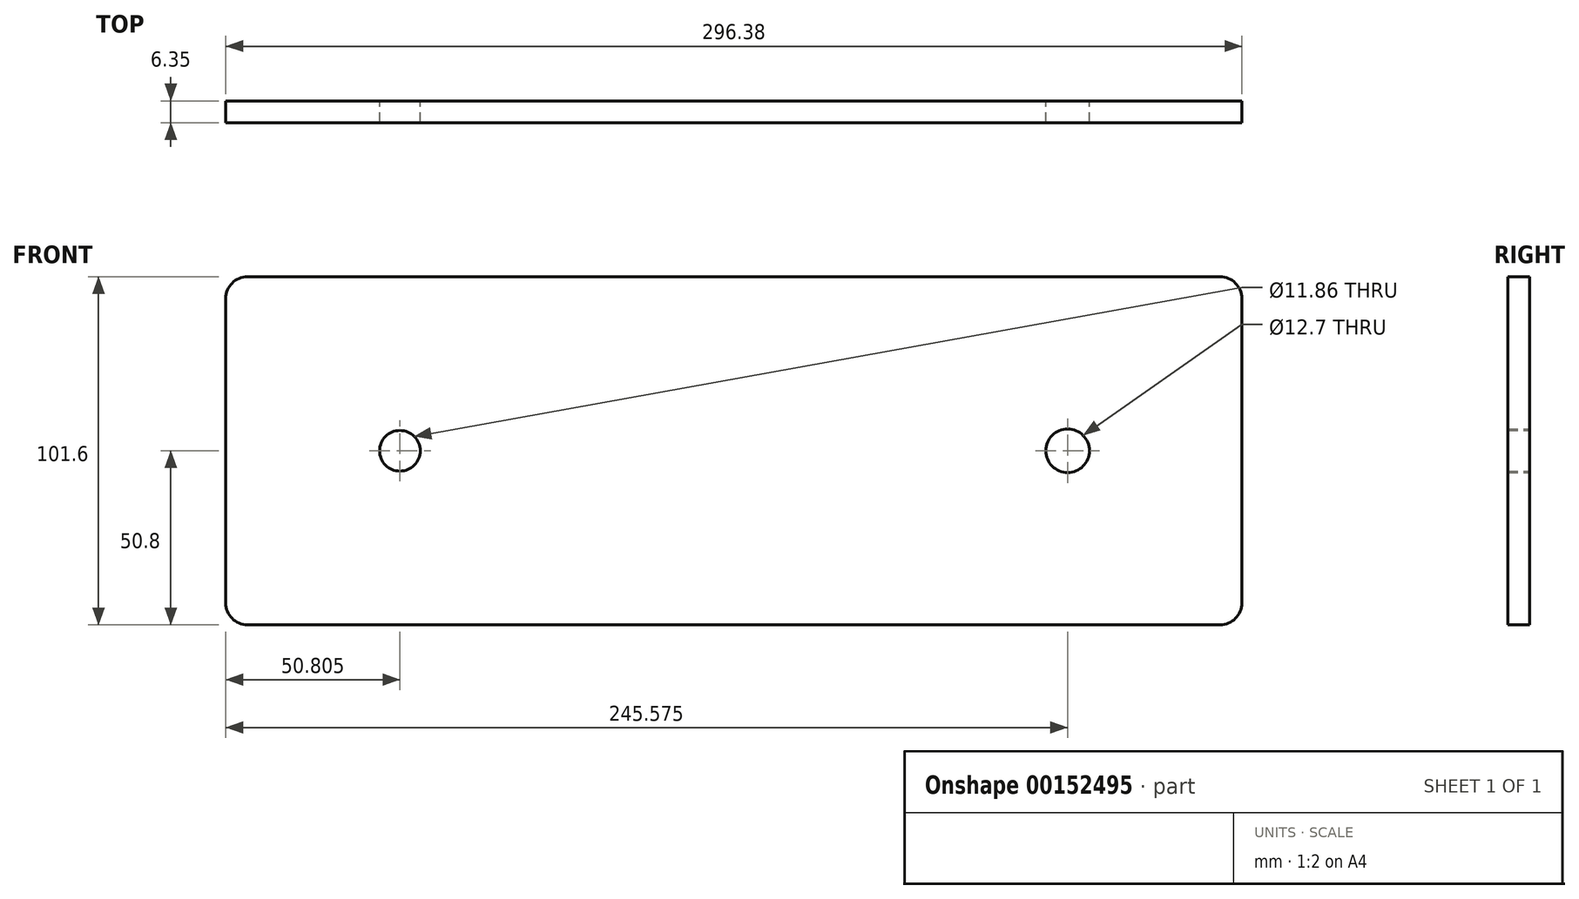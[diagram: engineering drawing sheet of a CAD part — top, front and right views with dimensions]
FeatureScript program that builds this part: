
annotation { "Feature Type Name" : "Feature", "Feature Type Description" : "" }
export const myFeature = defineFeature(function(context is Context, id is Id, definition is map)
    precondition{}
    {
        {
            var Q0;
            Q0=qCreatedBy(makeId("Front.planeOp"),FACE);
            var sketch = newSketch(context, id + "F0", { "sketchPlane" : qUnion([Q0])});
            skLineSegment(sketch, "E0.bottom", {"start": v(141.84, -50.8) * mm, "end": v(-141.84, -50.8) * mm});
            skLineSegment(sketch, "E0.top", {"start": v(141.84, 50.8) * mm, "end": v(-141.84, 50.8) * mm});
            skLineSegment(sketch, "E0.left", {"start": v(148.19, -44.45) * mm, "end": v(148.19, 44.45) * mm});
            skLineSegment(sketch, "E0.right", {"start": v(-148.19, -44.45) * mm, "end": v(-148.19, 44.45) * mm});
            skPoint(sketch, "E0.middle", {"position": v(0, 0) * mm});
            skCircle(sketch, "E1", {"center": v(-97.39, 0) * mm, "radius": 5.93 * mm});
            skCircle(sketch, "E2", {"center": v(97.39, 0) * mm, "radius": 6.35 * mm});
            skPoint(sketch, "E3.visualSharp", {"position": v(148.19, 50.8) * mm});
            skArc(sketch, "E3.filletArc", {"start": v(148.19, 44.45) * mm, "mid": v(146.33, 48.94) * mm, "end": v(141.84, 50.8) * mm});
            skPoint(sketch, "E4.visualSharp", {"position": v(148.19, -50.8) * mm});
            skArc(sketch, "E4.filletArc", {"start": v(141.84, -50.8) * mm, "mid": v(146.33, -48.94) * mm, "end": v(148.19, -44.45) * mm});
            skPoint(sketch, "E5.visualSharp", {"position": v(-148.19, -50.8) * mm});
            skArc(sketch, "E5.filletArc", {"start": v(-148.19, -44.45) * mm, "mid": v(-146.33, -48.94) * mm, "end": v(-141.84, -50.8) * mm});
            skPoint(sketch, "E6.visualSharp", {"position": v(-148.19, 50.8) * mm});
            skArc(sketch, "E6.filletArc", {"start": v(-141.84, 50.8) * mm, "mid": v(-146.33, 48.94) * mm, "end": v(-148.19, 44.45) * mm});
            skSolve(sketch);
        }
        {
            var Q0;
            Q0 = qSketchRegion(id + "F0", true);
            extrude(context, id + "F1", {"entities" : qUnion([Q0]), "depth" : 6.35 * mm});
        }
    });
